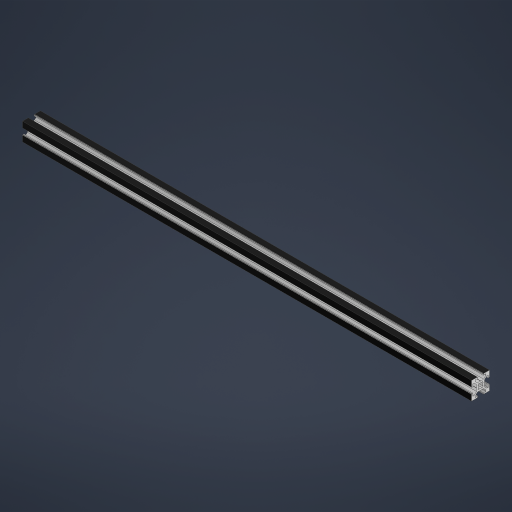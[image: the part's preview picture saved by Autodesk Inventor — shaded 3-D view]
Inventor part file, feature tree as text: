
AUTODESK INVENTOR PART (.ipt)
format: ipt  version: 2024.2 (Build 282272000, 272)  size: 330,240 bytes
history: native  units: mm
features: extrude x1, sketch x1
ambient origin geometry x8: Origin, YZ Plane, XZ Plane, XY Plane, X Axis, Y Axis, Z Axis, Center Point
bodies: Solid1 (feature_tree)
feature tree (2):
  extrude  "Extrusion1"  Depth=0.5mm
  sketch  "Sketch1"  dims[d2=6.5mm d3=0.5mm d4=4.0mm d5=3.465mm d6=5.48mm d7=0.795mm d8=0.305mm d9=2.95mm d11=0.75mm d14=45.0deg d15=10.0mm d16=1.0mm d17=3.0mm d18=45.0deg d19=40.0mm d21=360.0deg d23=500.0mm d24=0.0mm]
